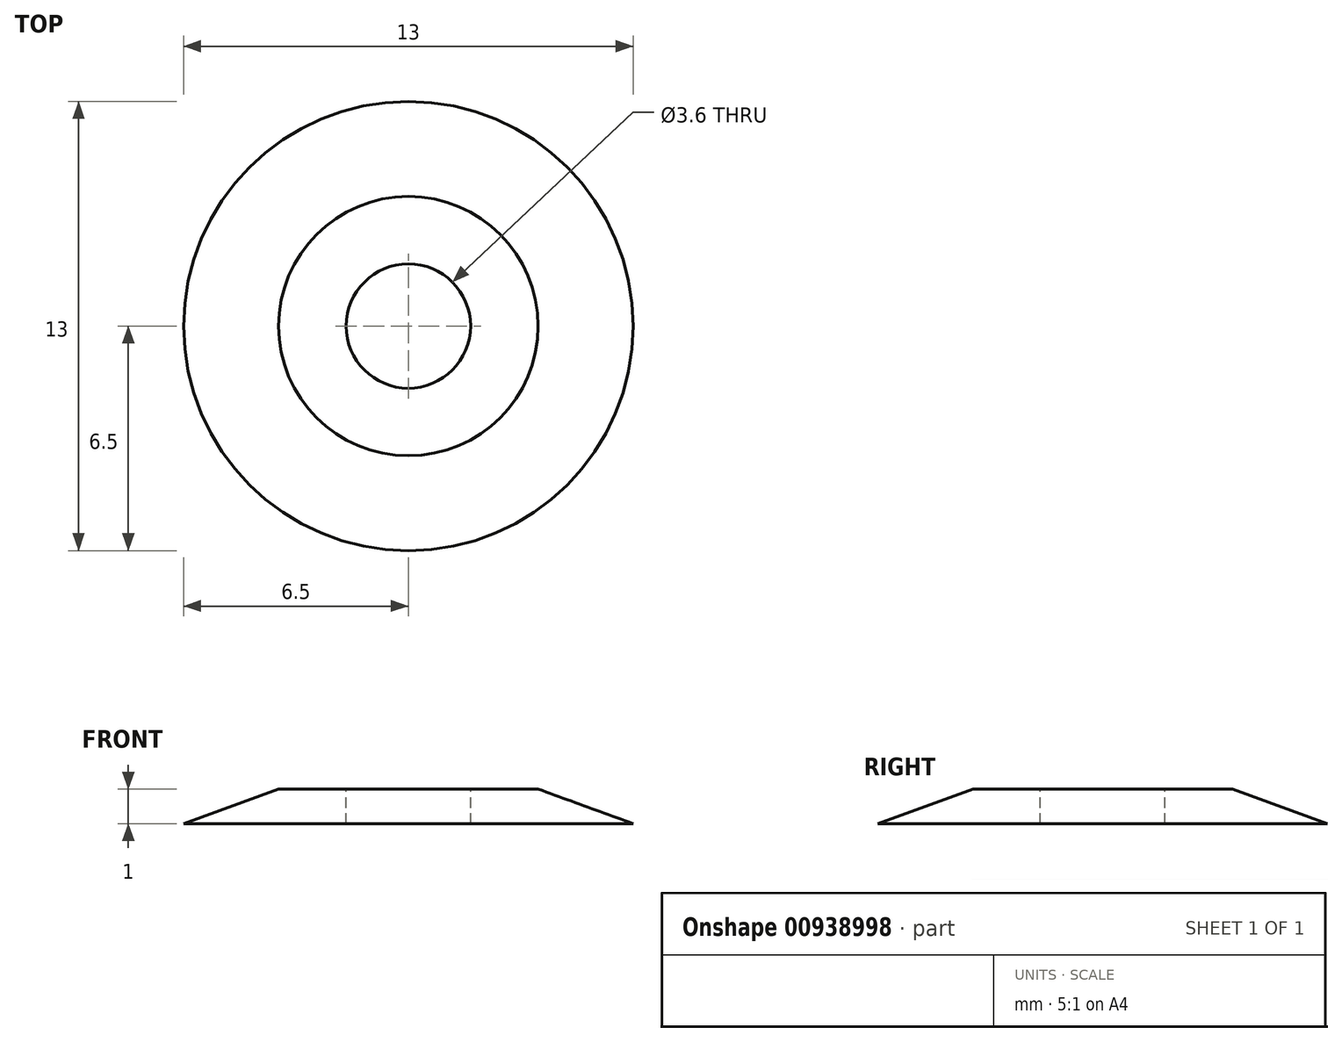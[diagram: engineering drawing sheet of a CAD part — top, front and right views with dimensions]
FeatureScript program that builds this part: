
annotation { "Feature Type Name" : "Feature", "Feature Type Description" : "" }
export const myFeature = defineFeature(function(context is Context, id is Id, definition is map)
    precondition{}
    {
        {
            var Q0;
            Q0=qCreatedBy(makeId("Top.planeOp"),FACE);
            var sketch = newSketch(context, id + "F0", { "sketchPlane" : qUnion([Q0])});
            skCircle(sketch, "E0", {"center": v(0, 0) * mm, "radius": 6.5 * mm});
            skSolve(sketch);
        }
        {
            var Q0;
            Q0=makeQuery(id+"F0.imprint","IMPRINT",FACE,{"disambiguationData":[TD([[makeQuery(id+"F0.imprint","IMPRINT",EDGE,{"derivedFrom":sQuery(id+"F0.wireOp",EDGE,"E0")}),1.0]])]});
            extrude(context, id + "F1", {"entities" : qUnion([Q0]), "depth" : 1 * mm, "offsetDistance" : 25 * mm, "hasDraft" : true, "draftAngle" : 70 * degree, "draftPullDirection" : true});
        }
        {
            var Q0;
            Q0=makeQuery(id+"F1.opExtrude","CAP_FACE",FACE,{"disambiguationData":[OSD([sQuery(id+"F0.wireOp",EDGE,"E0")])],"isStart":false});
            var sketch = newSketch(context, id + "F2", { "sketchPlane" : qUnion([Q0])});
            skCircle(sketch, "E1", {"center": v(0, 0) * mm, "radius": 1.8 * mm});
            skSolve(sketch);
        }
        {
            var Q0;
            Q0 = qSketchRegion(id + "F2", true);
            extrude(context, id + "F3", {"entities" : qUnion([Q0]), "operationType" : NewBodyOperationType.REMOVE, "oppositeDirection" : true, "depth" : 25 * mm, "offsetDistance" : 25 * mm});
        }
    });
